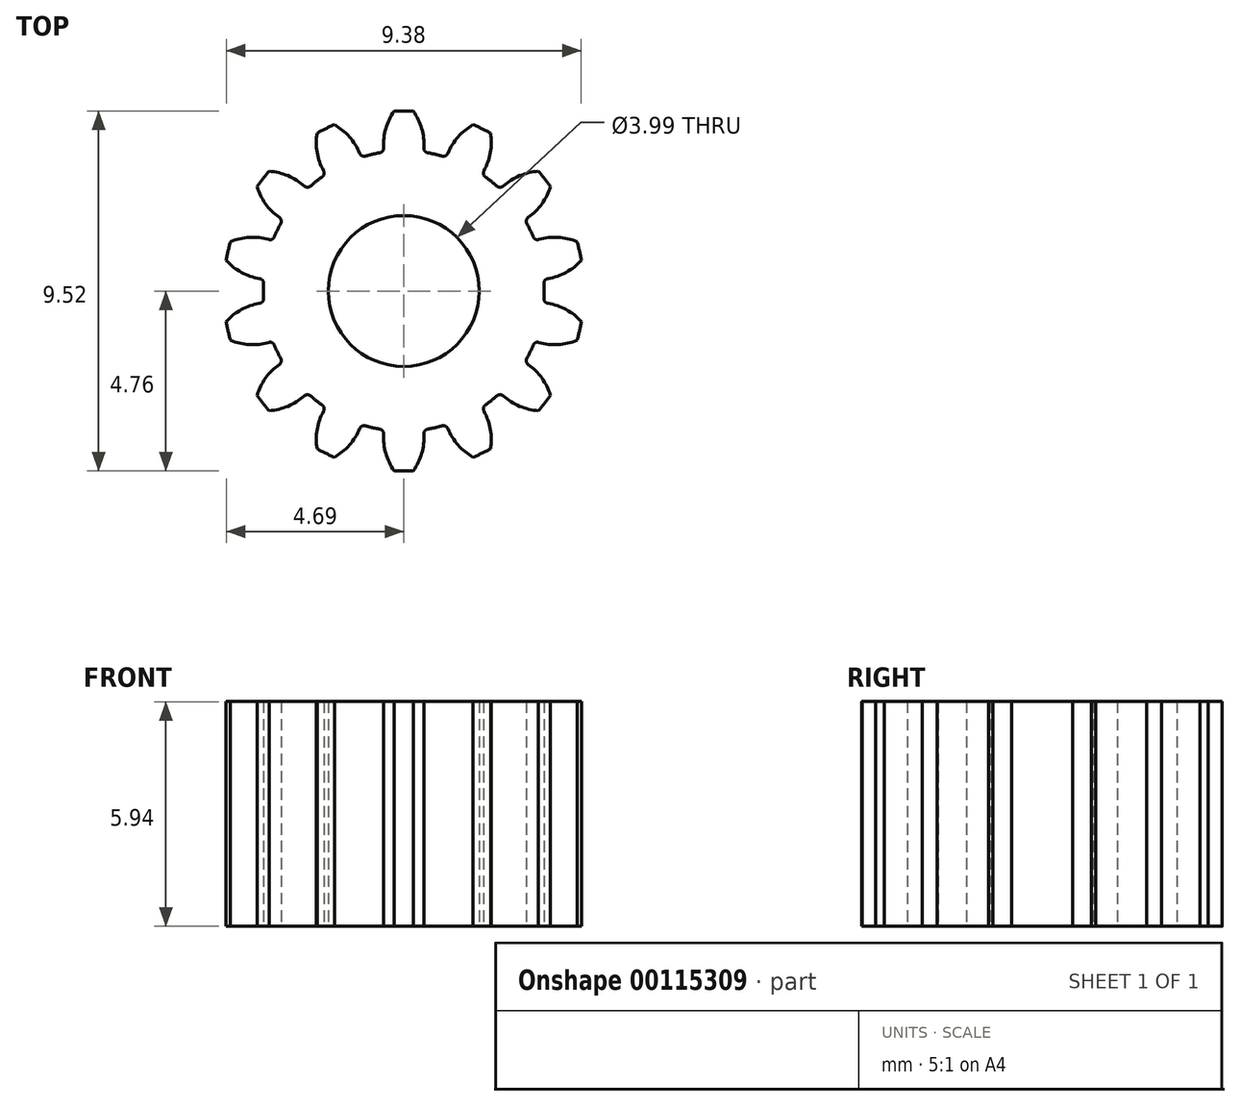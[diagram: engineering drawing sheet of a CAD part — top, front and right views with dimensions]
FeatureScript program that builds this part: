
annotation { "Feature Type Name" : "Feature", "Feature Type Description" : "" }
export const myFeature = defineFeature(function(context is Context, id is Id, definition is map)
    precondition{}
    {
        {
            var Q0;
            Q0=qCreatedBy(makeId("Top.planeOp"),FACE);
            var sketch = newSketch(context, id + "F0", { "sketchPlane" : qUnion([Q0])});
            skArc(sketch, "E0", {"start": v(1.01, 3.57) * mm, "mid": v(0.83, 3.62) * mm, "end": v(0.64, 3.65) * mm});
            skCircle(sketch, "E1", {"center": v(0, 0) * mm, "radius": 2 * mm});
            skArc(sketch, "E2", {"start": v(-3.56, 3.16) * mm, "mid": v(-3.72, 2.97) * mm, "end": v(-3.88, 2.77) * mm});
            skArc(sketch, "E3", {"start": v(-0.64, 3.65) * mm, "mid": v(-0.56, 3.7) * mm, "end": v(-0.53, 3.79) * mm});
            skArc(sketch, "E4", {"start": v(-0.25, 4.76) * mm, "mid": v(-0.47, 4.3) * mm, "end": v(-0.53, 3.79) * mm});
            skLineSegment(sketch, "E5", {"start": v(0, 0) * mm, "end": v(-1.06, 4.64) * mm, "construction": true});
            skArc(sketch, "E6.MirrorCS", {"start": v(0.25, 4.76) * mm, "mid": v(0.47, 4.3) * mm, "end": v(0.53, 3.79) * mm});
            skArc(sketch, "E7.MirrorCS", {"start": v(0.64, 3.65) * mm, "mid": v(0.56, 3.7) * mm, "end": v(0.53, 3.79) * mm});
            skArc(sketch, "E8.1.0", {"start": v(-1.83, 4.4) * mm, "mid": v(-1.44, 4.08) * mm, "end": v(-1.17, 3.64) * mm});
            skArc(sketch, "E8.1.1", {"start": v(-1.01, 3.57) * mm, "mid": v(-1.1, 3.58) * mm, "end": v(-1.17, 3.64) * mm});
            skArc(sketch, "E8.1.2", {"start": v(-2.3, 4.17) * mm, "mid": v(-2.3, 3.66) * mm, "end": v(-2.12, 3.18) * mm});
            skArc(sketch, "E8.1.3", {"start": v(-2.16, 3.02) * mm, "mid": v(-2.1, 3.1) * mm, "end": v(-2.12, 3.18) * mm});
            skArc(sketch, "E8.2.0", {"start": v(-3.56, 3.16) * mm, "mid": v(-3.06, 3.05) * mm, "end": v(-2.63, 2.78) * mm});
            skArc(sketch, "E8.2.1", {"start": v(-2.46, 2.77) * mm, "mid": v(-2.55, 2.74) * mm, "end": v(-2.63, 2.78) * mm});
            skArc(sketch, "E8.2.2", {"start": v(-3.88, 2.77) * mm, "mid": v(-3.65, 2.3) * mm, "end": v(-3.3, 1.95) * mm});
            skArc(sketch, "E8.2.3", {"start": v(-3.25, 1.78) * mm, "mid": v(-3.24, 1.87) * mm, "end": v(-3.3, 1.95) * mm});
            skArc(sketch, "E8.3.0", {"start": v(-4.58, 1.3) * mm, "mid": v(-4.08, 1.42) * mm, "end": v(-3.57, 1.36) * mm});
            skArc(sketch, "E8.3.1", {"start": v(-3.42, 1.43) * mm, "mid": v(-3.48, 1.37) * mm, "end": v(-3.57, 1.36) * mm});
            skArc(sketch, "E8.3.2", {"start": v(-4.7, 0.81) * mm, "mid": v(-4.3, 0.5) * mm, "end": v(-3.8, 0.33) * mm});
            skArc(sketch, "E8.3.3", {"start": v(-3.7, 0.2) * mm, "mid": v(-3.73, 0.28) * mm, "end": v(-3.8, 0.33) * mm});
            skArc(sketch, "E8.4.0", {"start": v(-4.7, -0.81) * mm, "mid": v(-4.3, -0.5) * mm, "end": v(-3.8, -0.33) * mm});
            skArc(sketch, "E8.4.1", {"start": v(-3.7, -0.2) * mm, "mid": v(-3.73, -0.28) * mm, "end": v(-3.8, -0.33) * mm});
            skArc(sketch, "E8.4.2", {"start": v(-4.58, -1.3) * mm, "mid": v(-4.08, -1.42) * mm, "end": v(-3.57, -1.36) * mm});
            skArc(sketch, "E8.4.3", {"start": v(-3.42, -1.43) * mm, "mid": v(-3.48, -1.37) * mm, "end": v(-3.57, -1.36) * mm});
            skArc(sketch, "E8.5.0", {"start": v(-3.88, -2.77) * mm, "mid": v(-3.65, -2.3) * mm, "end": v(-3.3, -1.95) * mm});
            skArc(sketch, "E8.5.1", {"start": v(-3.25, -1.78) * mm, "mid": v(-3.24, -1.87) * mm, "end": v(-3.3, -1.95) * mm});
            skArc(sketch, "E8.5.2", {"start": v(-3.56, -3.16) * mm, "mid": v(-3.06, -3.05) * mm, "end": v(-2.63, -2.78) * mm});
            skArc(sketch, "E8.5.3", {"start": v(-2.46, -2.77) * mm, "mid": v(-2.55, -2.74) * mm, "end": v(-2.63, -2.78) * mm});
            skArc(sketch, "E8.6.0", {"start": v(-2.3, -4.17) * mm, "mid": v(-2.3, -3.66) * mm, "end": v(-2.12, -3.18) * mm});
            skArc(sketch, "E8.6.1", {"start": v(-2.16, -3.02) * mm, "mid": v(-2.1, -3.1) * mm, "end": v(-2.12, -3.18) * mm});
            skArc(sketch, "E8.6.2", {"start": v(-1.83, -4.4) * mm, "mid": v(-1.44, -4.08) * mm, "end": v(-1.17, -3.64) * mm});
            skArc(sketch, "E8.6.3", {"start": v(-1.01, -3.57) * mm, "mid": v(-1.1, -3.58) * mm, "end": v(-1.17, -3.64) * mm});
            skArc(sketch, "E8.7.0", {"start": v(-0.25, -4.76) * mm, "mid": v(-0.47, -4.3) * mm, "end": v(-0.53, -3.79) * mm});
            skArc(sketch, "E8.7.1", {"start": v(-0.64, -3.65) * mm, "mid": v(-0.56, -3.7) * mm, "end": v(-0.53, -3.79) * mm});
            skArc(sketch, "E8.7.2", {"start": v(0.25, -4.76) * mm, "mid": v(0.47, -4.3) * mm, "end": v(0.53, -3.79) * mm});
            skArc(sketch, "E8.7.3", {"start": v(0.63, -3.65) * mm, "mid": v(0.56, -3.7) * mm, "end": v(0.53, -3.79) * mm});
            skArc(sketch, "E8.8.0", {"start": v(1.83, -4.4) * mm, "mid": v(1.44, -4.08) * mm, "end": v(1.17, -3.64) * mm});
            skArc(sketch, "E8.8.1", {"start": v(1.01, -3.57) * mm, "mid": v(1.1, -3.58) * mm, "end": v(1.17, -3.64) * mm});
            skArc(sketch, "E8.8.2", {"start": v(2.3, -4.17) * mm, "mid": v(2.3, -3.66) * mm, "end": v(2.12, -3.18) * mm});
            skArc(sketch, "E8.8.3", {"start": v(2.16, -3.02) * mm, "mid": v(2.1, -3.1) * mm, "end": v(2.12, -3.18) * mm});
            skArc(sketch, "E8.9.0", {"start": v(3.56, -3.16) * mm, "mid": v(3.06, -3.05) * mm, "end": v(2.63, -2.78) * mm});
            skArc(sketch, "E8.9.1", {"start": v(2.46, -2.77) * mm, "mid": v(2.55, -2.74) * mm, "end": v(2.63, -2.78) * mm});
            skArc(sketch, "E8.9.2", {"start": v(3.88, -2.77) * mm, "mid": v(3.65, -2.3) * mm, "end": v(3.3, -1.95) * mm});
            skArc(sketch, "E8.9.3", {"start": v(3.25, -1.78) * mm, "mid": v(3.24, -1.87) * mm, "end": v(3.3, -1.95) * mm});
            skArc(sketch, "E8.10.0", {"start": v(4.58, -1.3) * mm, "mid": v(4.08, -1.42) * mm, "end": v(3.57, -1.36) * mm});
            skArc(sketch, "E8.10.1", {"start": v(3.42, -1.43) * mm, "mid": v(3.48, -1.37) * mm, "end": v(3.57, -1.36) * mm});
            skArc(sketch, "E8.10.2", {"start": v(4.7, -0.81) * mm, "mid": v(4.3, -0.5) * mm, "end": v(3.8, -0.33) * mm});
            skArc(sketch, "E8.10.3", {"start": v(3.7, -0.2) * mm, "mid": v(3.73, -0.28) * mm, "end": v(3.8, -0.33) * mm});
            skArc(sketch, "E8.11.0", {"start": v(4.7, 0.81) * mm, "mid": v(4.3, 0.5) * mm, "end": v(3.8, 0.33) * mm});
            skArc(sketch, "E8.11.1", {"start": v(3.7, 0.2) * mm, "mid": v(3.73, 0.28) * mm, "end": v(3.8, 0.33) * mm});
            skArc(sketch, "E8.11.2", {"start": v(4.58, 1.3) * mm, "mid": v(4.08, 1.42) * mm, "end": v(3.57, 1.36) * mm});
            skArc(sketch, "E8.11.3", {"start": v(3.42, 1.43) * mm, "mid": v(3.48, 1.37) * mm, "end": v(3.57, 1.36) * mm});
            skArc(sketch, "E8.12.0", {"start": v(3.88, 2.77) * mm, "mid": v(3.65, 2.3) * mm, "end": v(3.3, 1.95) * mm});
            skArc(sketch, "E8.12.1", {"start": v(3.25, 1.78) * mm, "mid": v(3.24, 1.87) * mm, "end": v(3.3, 1.95) * mm});
            skArc(sketch, "E8.12.2", {"start": v(3.56, 3.16) * mm, "mid": v(3.06, 3.05) * mm, "end": v(2.63, 2.78) * mm});
            skArc(sketch, "E8.12.3", {"start": v(2.46, 2.77) * mm, "mid": v(2.55, 2.74) * mm, "end": v(2.63, 2.78) * mm});
            skArc(sketch, "E8.13.0", {"start": v(2.3, 4.17) * mm, "mid": v(2.3, 3.66) * mm, "end": v(2.12, 3.18) * mm});
            skArc(sketch, "E8.13.1", {"start": v(2.16, 3.02) * mm, "mid": v(2.1, 3.1) * mm, "end": v(2.12, 3.18) * mm});
            skArc(sketch, "E8.13.2", {"start": v(1.83, 4.4) * mm, "mid": v(1.44, 4.08) * mm, "end": v(1.17, 3.64) * mm});
            skArc(sketch, "E8.13.3", {"start": v(1.01, 3.57) * mm, "mid": v(1.1, 3.58) * mm, "end": v(1.17, 3.64) * mm});
            skArc(sketch, "E9.trimOffspring", {"start": v(-1.83, 4.4) * mm, "mid": v(-2.07, 4.3) * mm, "end": v(-2.3, 4.17) * mm});
            skArc(sketch, "E10.trimOffspring", {"start": v(0.25, 4.76) * mm, "mid": v(0, 4.76) * mm, "end": v(-0.25, 4.76) * mm});
            skArc(sketch, "E11.trimOffspring", {"start": v(2.3, 4.17) * mm, "mid": v(2.07, 4.3) * mm, "end": v(1.83, 4.4) * mm});
            skArc(sketch, "E12.trimOffspring", {"start": v(3.88, 2.77) * mm, "mid": v(3.72, 2.97) * mm, "end": v(3.56, 3.16) * mm});
            skArc(sketch, "E13.trimOffspring", {"start": v(4.7, 0.81) * mm, "mid": v(4.64, 1.06) * mm, "end": v(4.58, 1.3) * mm});
            skArc(sketch, "E14.trimOffspring", {"start": v(4.58, -1.3) * mm, "mid": v(4.64, -1.06) * mm, "end": v(4.7, -0.81) * mm});
            skArc(sketch, "E15.trimOffspring", {"start": v(3.56, -3.16) * mm, "mid": v(3.72, -2.97) * mm, "end": v(3.88, -2.77) * mm});
            skArc(sketch, "E16.trimOffspring", {"start": v(1.83, -4.4) * mm, "mid": v(2.07, -4.3) * mm, "end": v(2.3, -4.17) * mm});
            skArc(sketch, "E17.trimOffspring", {"start": v(-0.25, -4.76) * mm, "mid": v(0, -4.76) * mm, "end": v(0.25, -4.76) * mm});
            skArc(sketch, "E18.trimOffspring", {"start": v(-2.3, -4.17) * mm, "mid": v(-2.07, -4.3) * mm, "end": v(-1.83, -4.4) * mm});
            skArc(sketch, "E19.trimOffspring", {"start": v(-3.88, -2.77) * mm, "mid": v(-3.72, -2.97) * mm, "end": v(-3.56, -3.16) * mm});
            skArc(sketch, "E20.trimOffspring", {"start": v(-4.58, 1.3) * mm, "mid": v(-4.64, 1.06) * mm, "end": v(-4.7, 0.81) * mm});
            skArc(sketch, "E21.trimOffspring", {"start": v(-4.7, -0.81) * mm, "mid": v(-4.64, -1.06) * mm, "end": v(-4.58, -1.3) * mm});
            skArc(sketch, "E22.trimOffspring", {"start": v(2.46, 2.77) * mm, "mid": v(2.31, 2.9) * mm, "end": v(2.16, 3.02) * mm});
            skArc(sketch, "E23.trimOffspring", {"start": v(3.42, 1.43) * mm, "mid": v(3.34, 1.6) * mm, "end": v(3.25, 1.78) * mm});
            skArc(sketch, "E24.trimOffspring", {"start": v(3.7, -0.2) * mm, "mid": v(3.7, 0) * mm, "end": v(3.7, 0.2) * mm});
            skArc(sketch, "E25.trimOffspring", {"start": v(3.25, -1.78) * mm, "mid": v(3.34, -1.6) * mm, "end": v(3.42, -1.43) * mm});
            skArc(sketch, "E26.trimOffspring", {"start": v(0.63, -3.65) * mm, "mid": v(0.83, -3.62) * mm, "end": v(1.01, -3.57) * mm});
            skArc(sketch, "E27.trimOffspring", {"start": v(-1.01, -3.57) * mm, "mid": v(-0.83, -3.62) * mm, "end": v(-0.63, -3.65) * mm});
            skArc(sketch, "E28.trimOffspring", {"start": v(-2.46, -2.77) * mm, "mid": v(-2.31, -2.9) * mm, "end": v(-2.16, -3.02) * mm});
            skArc(sketch, "E29.trimOffspring", {"start": v(-3.42, -1.43) * mm, "mid": v(-3.34, -1.6) * mm, "end": v(-3.25, -1.78) * mm});
            skArc(sketch, "E30.trimOffspring", {"start": v(-3.7, 0.2) * mm, "mid": v(-3.7, 0) * mm, "end": v(-3.7, -0.2) * mm});
            skArc(sketch, "E31.trimOffspring", {"start": v(-3.25, 1.78) * mm, "mid": v(-3.34, 1.6) * mm, "end": v(-3.42, 1.43) * mm});
            skArc(sketch, "E32.trimOffspring", {"start": v(-2.16, 3.02) * mm, "mid": v(-2.31, 2.9) * mm, "end": v(-2.46, 2.77) * mm});
            skArc(sketch, "E33.trimOffspring", {"start": v(-0.64, 3.65) * mm, "mid": v(-0.83, 3.62) * mm, "end": v(-1.01, 3.57) * mm});
            skArc(sketch, "E34.trimOffspring", {"start": v(2.16, -3.02) * mm, "mid": v(2.31, -2.9) * mm, "end": v(2.46, -2.77) * mm});
            skSolve(sketch);
        }
        {
            var Q0;
            Q0=makeQuery(id+"F0.imprint","IMPRINT",FACE,{"disambiguationData":[TD([[makeQuery(id+"F0.imprint","IMPRINT",EDGE,{"derivedFrom":sQuery(id+"F0.wireOp",EDGE,"E0")}),1.0]])]});
            extrude(context, id + "F1", {"entities" : qUnion([Q0]), "depth" : 5.94 * mm});
        }
    });
